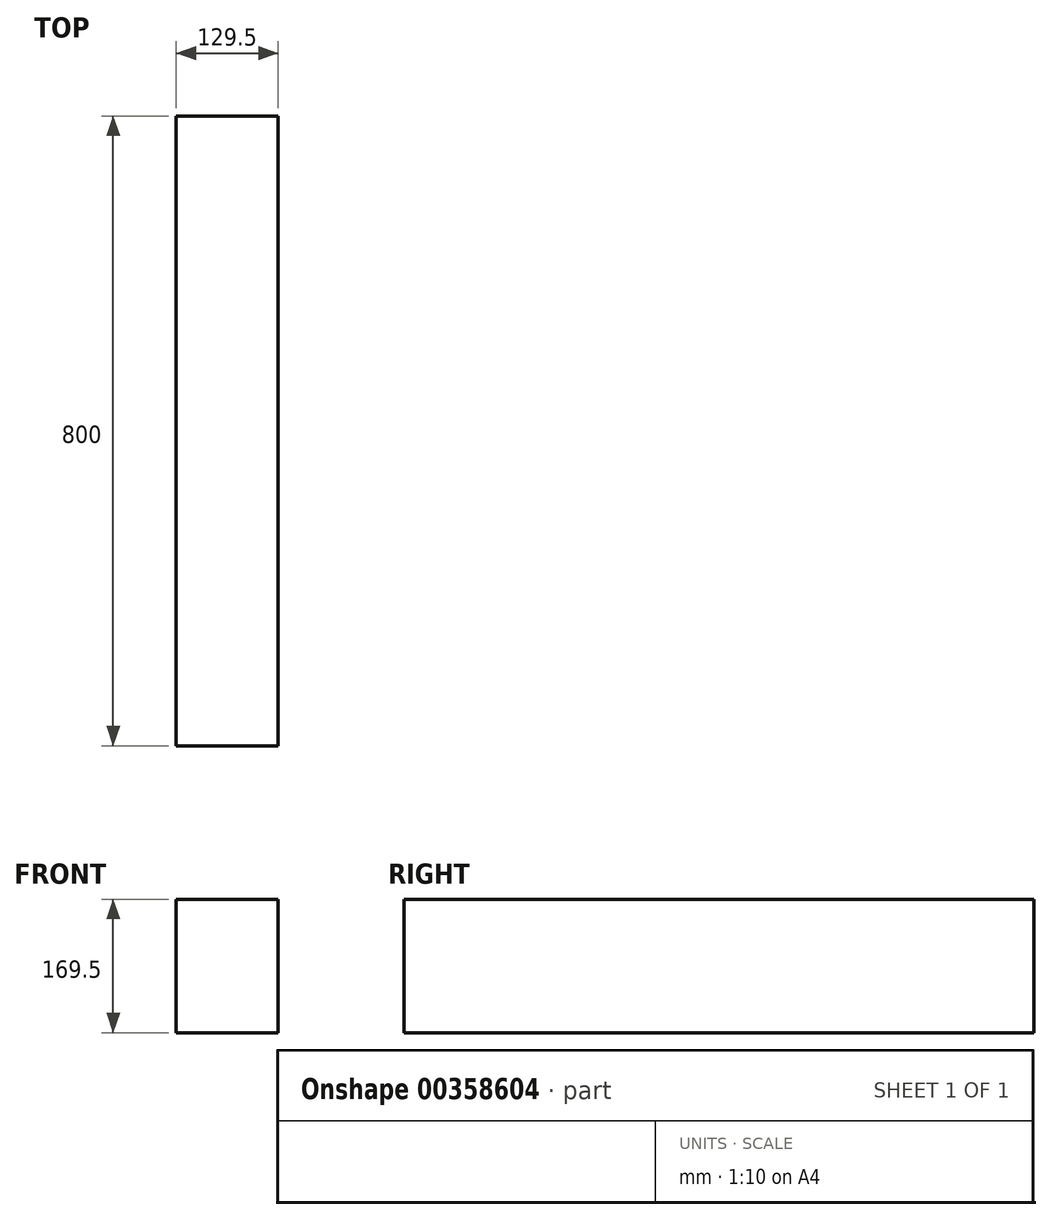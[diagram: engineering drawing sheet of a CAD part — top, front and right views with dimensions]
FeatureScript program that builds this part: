
annotation { "Feature Type Name" : "Feature", "Feature Type Description" : "" }
export const myFeature = defineFeature(function(context is Context, id is Id, definition is map)
    precondition{}
    {
        {
            var Q0;
            Q0=qCreatedBy(makeId("Front.planeOp"),FACE);
            var sketch = newSketch(context, id + "F0", { "sketchPlane" : qUnion([Q0])});
            skLineSegment(sketch, "E0.bottom", {"start": v(64.75, -84.75) * mm, "end": v(-64.75, -84.75) * mm});
            skLineSegment(sketch, "E0.top", {"start": v(64.75, 84.75) * mm, "end": v(-64.75, 84.75) * mm});
            skLineSegment(sketch, "E0.left", {"start": v(64.75, -84.75) * mm, "end": v(64.75, 84.75) * mm});
            skLineSegment(sketch, "E0.right", {"start": v(-64.75, -84.75) * mm, "end": v(-64.75, 84.75) * mm});
            skPoint(sketch, "E0.middle", {"position": v(0, 0) * mm});
            skSolve(sketch);
        }
        {
            var Q0;
            Q0 = qSketchRegion(id + "F0", true);
            extrude(context, id + "F1", {"entities" : qUnion([Q0]), "oppositeDirection" : true, "depth" : 800 * mm});
        }
    });
